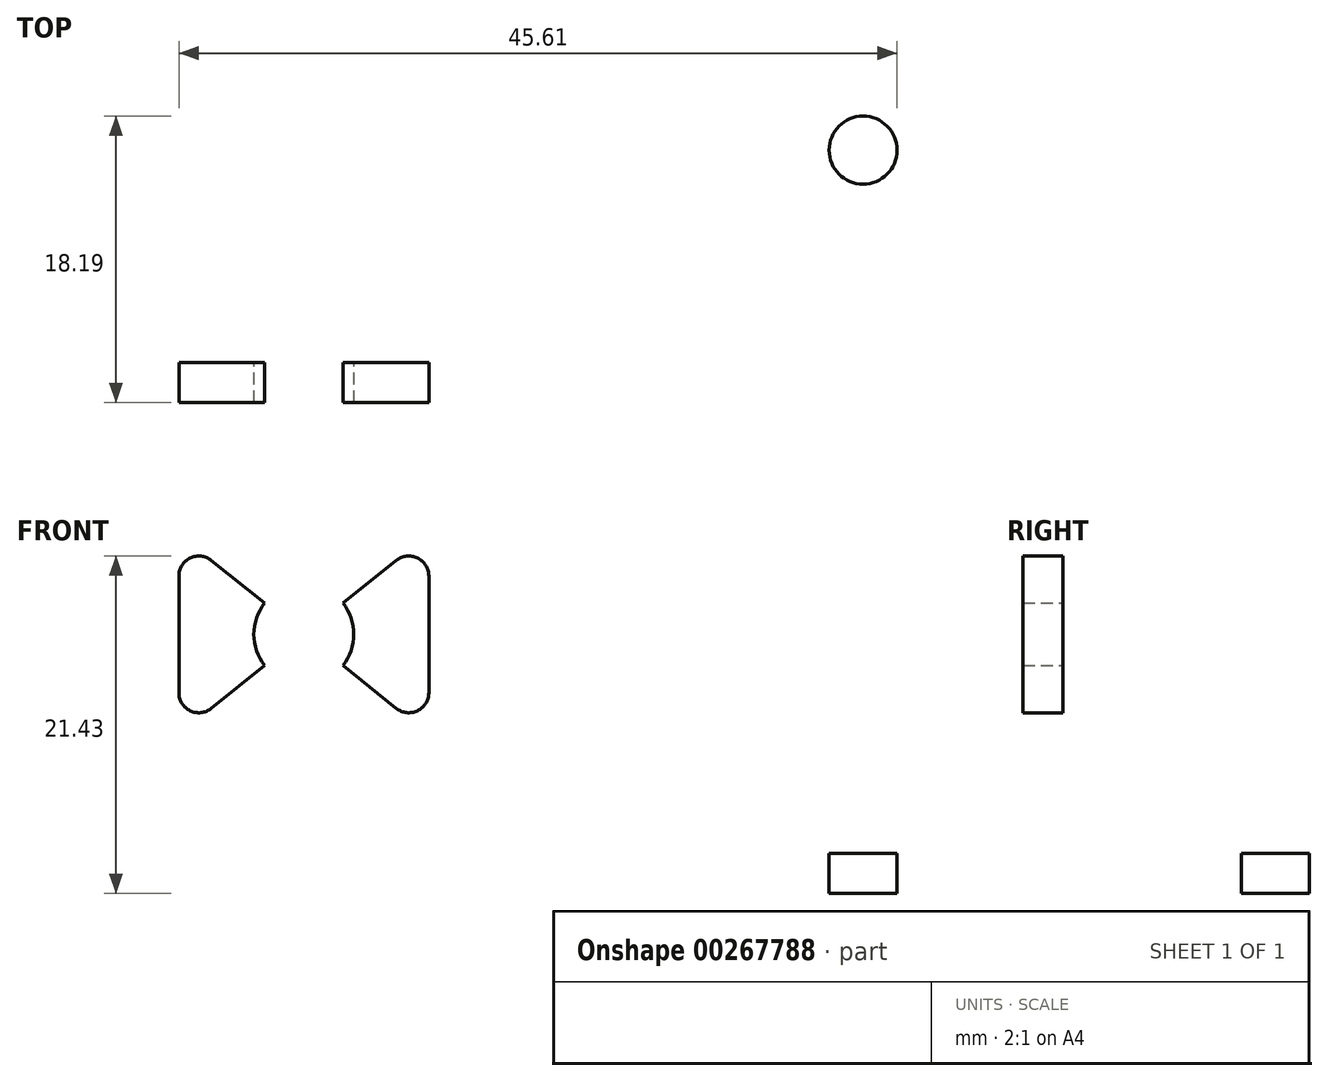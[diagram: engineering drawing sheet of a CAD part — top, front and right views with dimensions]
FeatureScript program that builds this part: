
annotation { "Feature Type Name" : "Feature", "Feature Type Description" : "" }
export const myFeature = defineFeature(function(context is Context, id is Id, definition is map)
    precondition{}
    {
        {
            var Q0;
            Q0=qCreatedBy(makeId("Front.planeOp"),FACE);
            var sketch = newSketch(context, id + "F0", { "sketchPlane" : qUnion([Q0])});
            skLineSegment(sketch, "E0", {"start": v(-52.62, 22.8) * mm, "end": v(-52.62, 10.1) * mm});
            skLineSegment(sketch, "E1", {"start": v(-52.62, 10.1) * mm, "end": v(-44.68, 16.45) * mm});
            skLineSegment(sketch, "E2", {"start": v(-44.68, 16.45) * mm, "end": v(-52.62, 22.8) * mm});
            skLineSegment(sketch, "E3", {"start": v(-44.68, 16.45) * mm, "end": v(-36.75, 22.8) * mm});
            skLineSegment(sketch, "E4", {"start": v(-36.75, 22.8) * mm, "end": v(-36.75, 10.1) * mm});
            skLineSegment(sketch, "E5", {"start": v(-36.75, 10.1) * mm, "end": v(-44.68, 16.45) * mm});
            skCircle(sketch, "E6", {"center": v(-44.68, 16.45) * mm, "radius": 3.18 * mm});
            skSolve(sketch);
        }
        {
            var Q0;
            {var subQ0=sQuery(id+"F0.wireOp",EDGE,"E4");Q0=makeQuery(id+"F0.imprint","IMPRINT",FACE,{"disambiguationData":[TD([[makeQuery(id+"F0.imprint","IMPRINT",EDGE,{"derivedFrom":subQ0}),-1.0]])]});}
            var Q1;
            {var subQ0=sQuery(id+"F0.wireOp",EDGE,"E0");Q1=makeQuery(id+"F0.imprint","IMPRINT",FACE,{"disambiguationData":[TD([[makeQuery(id+"F0.imprint","IMPRINT",EDGE,{"derivedFrom":subQ0}),1.0]])]});}
            extrude(context, id + "F1", {"entities" : qUnion([Q0, Q1]), "depth" : 2.54 * mm});
        }
        {
            var Q0;
            Q0=makeQuery(id+"F1.opExtrude","SWEPT_EDGE",EDGE,{"disambiguationData":[OSD([sQuery(id+"F0.wireOp",EDGE,"E0"),sQuery(id+"F0.wireOp",EDGE,"E1")])]});
            var Q1;
            Q1=makeQuery(id+"F1.opExtrude","SWEPT_EDGE",EDGE,{"disambiguationData":[OSD([sQuery(id+"F0.wireOp",EDGE,"E4"),sQuery(id+"F0.wireOp",EDGE,"E5")])]});
            var Q2;
            Q2=makeQuery(id+"F1.opExtrude","SWEPT_EDGE",EDGE,{"disambiguationData":[OSD([sQuery(id+"F0.wireOp",EDGE,"E3"),sQuery(id+"F0.wireOp",EDGE,"E4")])]});
            var Q3;
            Q3=makeQuery(id+"F1.opExtrude","SWEPT_EDGE",EDGE,{"disambiguationData":[OSD([sQuery(id+"F0.wireOp",EDGE,"E0"),sQuery(id+"F0.wireOp",EDGE,"E2")])]});
            fillet(context, id + "F2", {"entities" : qUnion([Q0, Q1, Q2, Q3]), "radius" : 1.27 * mm, "tangentPropagation" : true, "allowEdgeOverflow" : false});
        }
        {
            var Q0;
            Q0=qCreatedBy(makeId("Top.planeOp"),FACE);
            var sketch = newSketch(context, id + "F3", { "sketchPlane" : qUnion([Q0])});
            skCircle(sketch, "E7", {"center": v(-9.17, 13.49) * mm, "radius": 2.16 * mm});
            skSolve(sketch);
        }
        {
            var Q0;
            Q0=makeQuery(id+"F3.imprint","IMPRINT",FACE,{"disambiguationData":[TD([[makeQuery(id+"F3.imprint","IMPRINT",EDGE,{"derivedFrom":sQuery(id+"F3.wireOp",EDGE,"E7")}),1.0]])]});
            extrude(context, id + "F4", {"entities" : qUnion([Q0]), "depth" : 2.54 * mm});
        }
    });
